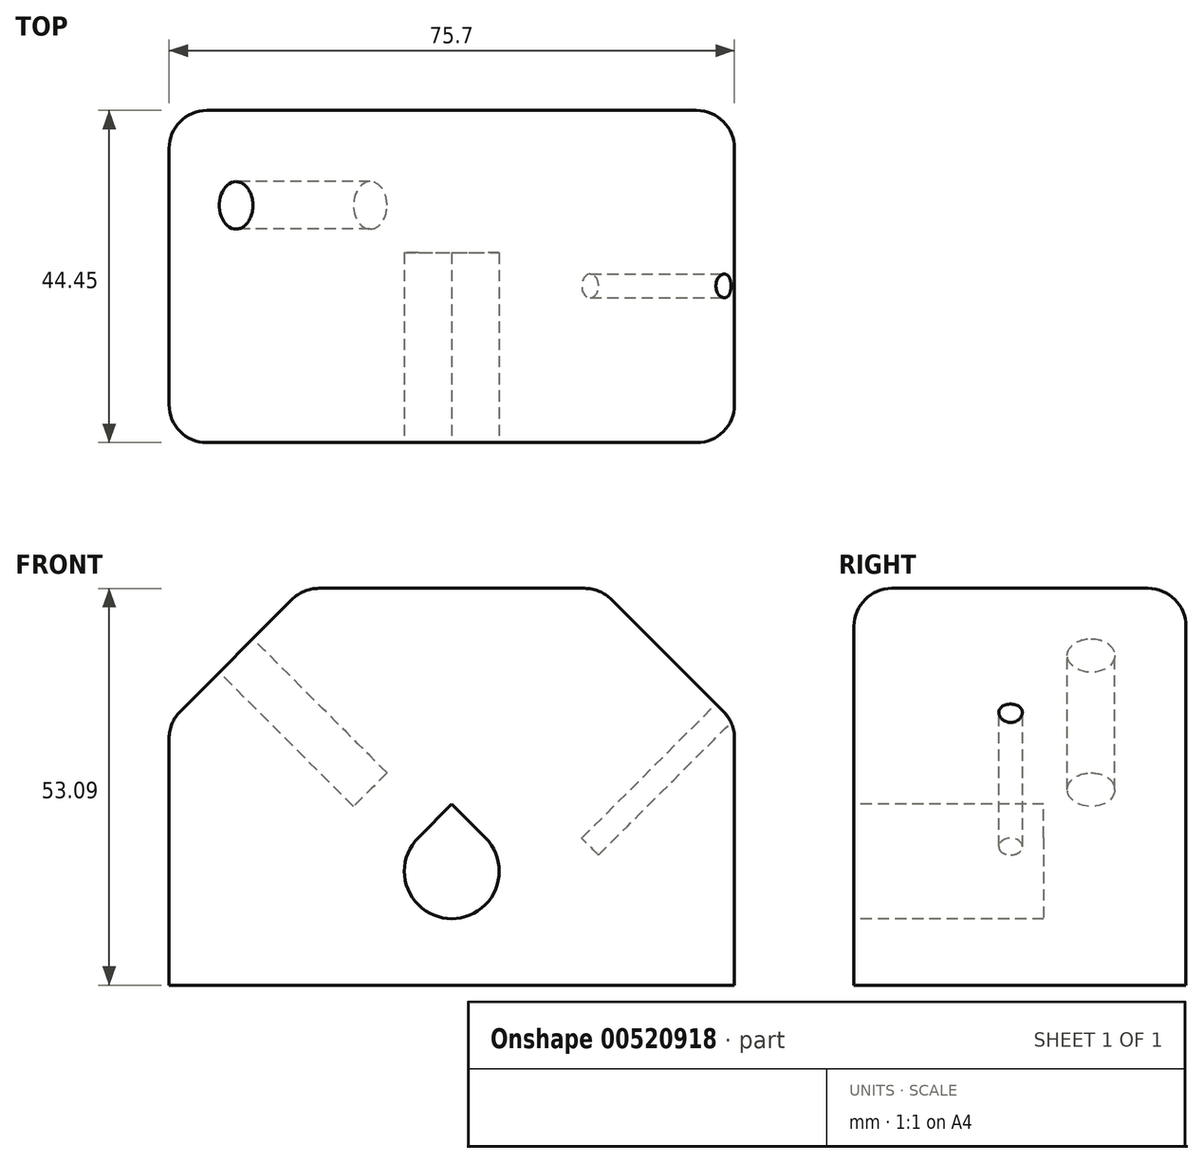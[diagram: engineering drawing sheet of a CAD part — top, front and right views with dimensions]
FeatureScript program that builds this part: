
annotation { "Feature Type Name" : "Feature", "Feature Type Description" : "" }
export const myFeature = defineFeature(function(context is Context, id is Id, definition is map)
    precondition{}
    {
        {
            var Q0;
            Q0=qCreatedBy(makeId("Front.planeOp"),FACE);
            var sketch = newSketch(context, id + "F0", { "sketchPlane" : qUnion([Q0])});
            skLineSegment(sketch, "E0", {"start": v(0, 0) * mm, "end": v(-37.85, 0) * mm});
            skLineSegment(sketch, "E1", {"start": v(-37.85, 0) * mm, "end": v(-37.85, 35.13) * mm});
            skLineSegment(sketch, "E2", {"start": v(-37.85, 35.13) * mm, "end": v(-19.9, 53.1) * mm});
            skLineSegment(sketch, "E3", {"start": v(-19.9, 53.1) * mm, "end": v(0, 53.1) * mm});
            skLineSegment(sketch, "E4", {"start": v(0, 53.1) * mm, "end": v(0, 0) * mm, "construction": true});
            skPoint(sketch, "E5", {"position": v(-28.87, 44.11) * mm});
            skPoint(sketch, "E6", {"position": v(-24.38, 48.6) * mm});
            skPoint(sketch, "E7", {"position": v(-33.36, 39.62) * mm});
            skLineSegment(sketch, "E8.MirrorCS", {"start": v(19.9, 53.1) * mm, "end": v(0, 53.1) * mm});
            skLineSegment(sketch, "E9.MirrorCS", {"start": v(37.85, 35.13) * mm, "end": v(19.9, 53.1) * mm});
            skPoint(sketch, "E10.MirrorP", {"position": v(28.87, 44.11) * mm});
            skLineSegment(sketch, "E11.MirrorCS", {"start": v(37.85, 0) * mm, "end": v(37.85, 35.13) * mm});
            skLineSegment(sketch, "E12.MirrorCS", {"start": v(0, 0) * mm, "end": v(37.85, 0) * mm});
            skLineSegment(sketch, "E13", {"start": v(-28.87, 44.11) * mm, "end": v(0, 15.24) * mm, "construction": true});
            skLineSegment(sketch, "E14", {"start": v(0, 15.24) * mm, "end": v(28.87, 44.11) * mm, "construction": true});
            skSolve(sketch);
        }
        {
            var Q0;
            Q0 = qSketchRegion(id + "F0", true);
            extrude(context, id + "F1", {"entities" : qUnion([Q0]), "depth" : 31.75 * mm, "offsetDistance" : 25.4 * mm, "hasSecondDirection" : true, "secondDirectionOppositeDirection" : true, "secondDirectionDepth" : 12.7 * mm});
        }
        {
            var Q0;
            Q0=makeQuery(id+"F1.opExtrude","SWEPT_FACE",FACE,{"disambiguationData":[OSD([sQuery(id+"F0.wireOp",EDGE,"E2")])]});
            var sketch = newSketch(context, id + "F2", { "sketchPlane" : qUnion([Q0])});
            skPoint(sketch, "E15.0", {"position": v(0, 10.78) * mm});
            skCircle(sketch, "E16", {"center": v(0, 10.78) * mm, "radius": 3.18 * mm});
            skSolve(sketch);
        }
        {
            var Q0;
            Q0 = qSketchRegion(id + "F2", true);
            extrude(context, id + "F3", {"entities" : qUnion([Q0]), "operationType" : NewBodyOperationType.REMOVE, "oppositeDirection" : true, "depth" : 25.4 * mm, "offsetDistance" : 25.4 * mm});
        }
        {
            var Q0;
            Q0=makeQuery(id+"F1.opExtrude","SWEPT_FACE",FACE,{"disambiguationData":[OSD([sQuery(id+"F0.wireOp",EDGE,"E9.MirrorCS")])]});
            var sketch = newSketch(context, id + "F4", { "sketchPlane" : qUnion([Q0])});
            skPoint(sketch, "E17.0", {"position": v(-10.78, 0) * mm});
            skCircle(sketch, "E18", {"center": v(-10.78, 0) * mm, "radius": 1.59 * mm});
            skSolve(sketch);
        }
        {
            var Q0;
            Q0 = qSketchRegion(id + "F4", true);
            extrude(context, id + "F5", {"entities" : qUnion([Q0]), "operationType" : NewBodyOperationType.REMOVE, "oppositeDirection" : true, "depth" : 25.4 * mm, "offsetDistance" : 25.4 * mm});
        }
        {
            var Q0;
            Q0=makeQuery(id+"F1.opExtrude","CAP_FACE",FACE,{"disambiguationData":[OSD([sQuery(id+"F0.wireOp",EDGE,"E0"),sQuery(id+"F0.wireOp",EDGE,"E1"),sQuery(id+"F0.wireOp",EDGE,"E2"),sQuery(id+"F0.wireOp",EDGE,"E3"),sQuery(id+"F0.wireOp",EDGE,"E8.MirrorCS"),sQuery(id+"F0.wireOp",EDGE,"E9.MirrorCS"),sQuery(id+"F0.wireOp",EDGE,"E11.MirrorCS"),sQuery(id+"F0.wireOp",EDGE,"E12.MirrorCS")])],"isStart":false});
            var sketch = newSketch(context, id + "F6", { "sketchPlane" : qUnion([Q0])});
            skPoint(sketch, "E19.0", {"position": v(0, 15.24) * mm});
            skArc(sketch, "E20", {"start": v(-4.5, 19.73) * mm, "mid": v(0, 8.9) * mm, "end": v(4.5, 19.73) * mm});
            skLineSegment(sketch, "E21.0", {"start": v(-28.87, 44.11) * mm, "end": v(0, 15.24) * mm, "construction": true});
            skLineSegment(sketch, "E21.1", {"start": v(0, 15.24) * mm, "end": v(28.87, 44.11) * mm, "construction": true});
            skLineSegment(sketch, "E22", {"start": v(-4.5, 19.73) * mm, "end": v(0, 24.22) * mm});
            skLineSegment(sketch, "E23", {"start": v(0, 24.22) * mm, "end": v(4.5, 19.73) * mm});
            skSolve(sketch);
        }
        {
            var Q0;
            Q0 = qSketchRegion(id + "F6", true);
            extrude(context, id + "F7", {"entities" : qUnion([Q0]), "operationType" : NewBodyOperationType.REMOVE, "oppositeDirection" : true, "depth" : 25.4 * mm, "offsetDistance" : 25.4 * mm});
        }
        {
            var Q0;
            Q0=makeQuery(id+"F1.opExtrude","CAP_EDGE",EDGE,{"disambiguationData":[OSD([sQuery(id+"F0.wireOp",EDGE,"E1")])],"isStart":true});
            var Q1;
            Q1=makeQuery(id+"F1.opExtrude","CAP_EDGE",EDGE,{"disambiguationData":[OSD([sQuery(id+"F0.wireOp",EDGE,"E2")])],"isStart":true});
            var Q2;
            Q2=makeQuery(id+"F1.opExtrude","CAP_EDGE",EDGE,{"disambiguationData":[OSD([sQuery(id+"F0.wireOp",EDGE,"E3"),sQuery(id+"F0.wireOp",EDGE,"E8.MirrorCS")])],"isStart":true});
            var Q3;
            Q3=makeQuery(id+"F1.opExtrude","CAP_EDGE",EDGE,{"disambiguationData":[OSD([sQuery(id+"F0.wireOp",EDGE,"E9.MirrorCS")])],"isStart":true});
            var Q4;
            Q4=makeQuery(id+"F1.opExtrude","CAP_EDGE",EDGE,{"disambiguationData":[OSD([sQuery(id+"F0.wireOp",EDGE,"E11.MirrorCS")])],"isStart":true});
            var Q5;
            Q5=makeQuery(id+"F1.opExtrude","SWEPT_EDGE",EDGE,{"disambiguationData":[OSD([sQuery(id+"F0.wireOp",EDGE,"E2"),sQuery(id+"F0.wireOp",EDGE,"E3")])]});
            var Q6;
            Q6=makeQuery(id+"F1.opExtrude","SWEPT_EDGE",EDGE,{"disambiguationData":[OSD([sQuery(id+"F0.wireOp",EDGE,"E1"),sQuery(id+"F0.wireOp",EDGE,"E2")])]});
            var Q7;
            Q7=makeQuery(id+"F1.opExtrude","CAP_EDGE",EDGE,{"disambiguationData":[OSD([sQuery(id+"F0.wireOp",EDGE,"E2")])],"isStart":false});
            var Q8;
            Q8=makeQuery(id+"F1.opExtrude","CAP_EDGE",EDGE,{"disambiguationData":[OSD([sQuery(id+"F0.wireOp",EDGE,"E1")])],"isStart":false});
            var Q9;
            Q9=makeQuery(id+"F1.opExtrude","CAP_EDGE",EDGE,{"disambiguationData":[OSD([sQuery(id+"F0.wireOp",EDGE,"E3"),sQuery(id+"F0.wireOp",EDGE,"E8.MirrorCS")])],"isStart":false});
            var Q10;
            Q10=makeQuery(id+"F1.opExtrude","SWEPT_EDGE",EDGE,{"disambiguationData":[OSD([sQuery(id+"F0.wireOp",EDGE,"E8.MirrorCS"),sQuery(id+"F0.wireOp",EDGE,"E9.MirrorCS")])]});
            var Q11;
            Q11=makeQuery(id+"F1.opExtrude","CAP_EDGE",EDGE,{"disambiguationData":[OSD([sQuery(id+"F0.wireOp",EDGE,"E9.MirrorCS")])],"isStart":false});
            var Q12;
            Q12=makeQuery(id+"F1.opExtrude","CAP_EDGE",EDGE,{"disambiguationData":[OSD([sQuery(id+"F0.wireOp",EDGE,"E11.MirrorCS")])],"isStart":false});
            var Q13;
            Q13=makeQuery(id+"F1.opExtrude","SWEPT_EDGE",EDGE,{"disambiguationData":[OSD([sQuery(id+"F0.wireOp",EDGE,"E9.MirrorCS"),sQuery(id+"F0.wireOp",EDGE,"E11.MirrorCS")])]});
            fillet(context, id + "F8", {"entities" : qUnion([Q0, Q1, Q2, Q3, Q4, Q5, Q6, Q7, Q8, Q9, Q10, Q11, Q12, Q13]), "radius" : 5.08 * mm, "tangentPropagation" : true, "allowEdgeOverflow" : false});
        }
    });
